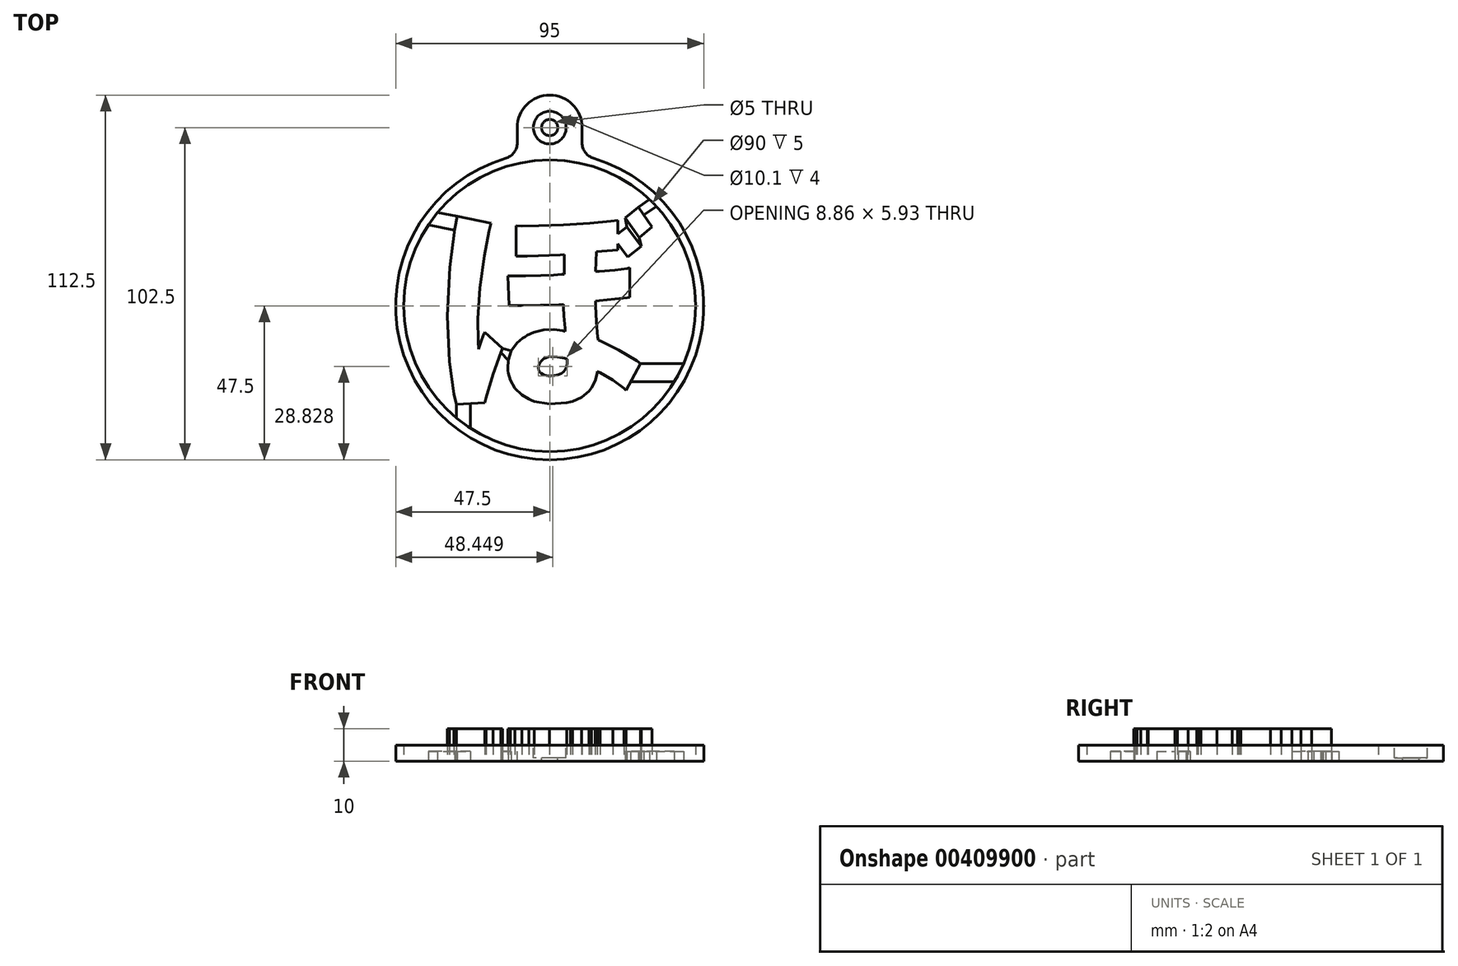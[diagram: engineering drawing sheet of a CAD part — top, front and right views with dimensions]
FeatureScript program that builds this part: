
annotation { "Feature Type Name" : "Feature", "Feature Type Description" : "" }
export const myFeature = defineFeature(function(context is Context, id is Id, definition is map)
    precondition{}
    {
        {
            var Q0;
            Q0=qCreatedBy(makeId("Top.planeOp"),FACE);
            var sketch = newSketch(context, id + "F0", { "sketchPlane" : qUnion([Q0])});
            skCircle(sketch, "E0", {"center": v(0, 0) * mm, "radius": 45 * mm});
            skCircle(sketch, "E1", {"center": v(0, 0) * mm, "radius": 47.5 * mm});
            skSolve(sketch);
        }
        {
            var Q0;
            Q0=qCreatedBy(makeId("Top.planeOp"),FACE);
            var sketch = newSketch(context, id + "F1", { "sketchPlane" : qUnion([Q0])});
            skLineSegment(sketch, "E2", {"start": v(27.39, 30.45) * mm, "end": v(31.52, 24.4) * mm});
            skLineSegment(sketch, "E3", {"start": v(31.52, 24.4) * mm, "end": v(27.67, 21.08) * mm});
            skLineSegment(sketch, "E4", {"start": v(27.67, 21.08) * mm, "end": v(23.26, 27.15) * mm});
            skLineSegment(sketch, "E5", {"start": v(23.26, 27.15) * mm, "end": v(27.39, 30.45) * mm});
            skLineSegment(sketch, "E6", {"start": v(-10.37, 24.67) * mm, "end": v(-8.61, 24.63) * mm});
            skLineSegment(sketch, "E7", {"start": v(-8.61, 24.63) * mm, "end": v(-3.34, 24.67) * mm});
            skLineSegment(sketch, "E8", {"start": v(-3.34, 24.67) * mm, "end": v(4.24, 24.94) * mm});
            skLineSegment(sketch, "E9", {"start": v(4.24, 24.94) * mm, "end": v(12.37, 25.5) * mm});
            skLineSegment(sketch, "E10", {"start": v(12.37, 25.5) * mm, "end": v(18.88, 26.09) * mm});
            skLineSegment(sketch, "E11", {"start": v(18.88, 26.09) * mm, "end": v(21.05, 26.32) * mm});
            skLineSegment(sketch, "E12", {"start": v(21.05, 26.32) * mm, "end": v(21.05, 22.19) * mm});
            skLineSegment(sketch, "E13", {"start": v(21.05, 22.19) * mm, "end": v(23.8, 24.4) * mm});
            skLineSegment(sketch, "E14", {"start": v(23.8, 24.4) * mm, "end": v(28.22, 18.33) * mm});
            skLineSegment(sketch, "E15", {"start": v(28.22, 18.33) * mm, "end": v(24.08, 15.02) * mm});
            skLineSegment(sketch, "E16", {"start": v(24.08, 15.02) * mm, "end": v(21.05, 19.15) * mm});
            skLineSegment(sketch, "E17", {"start": v(21.05, 19.15) * mm, "end": v(21.05, 17.23) * mm});
            skLineSegment(sketch, "E18", {"start": v(21.05, 17.23) * mm, "end": v(14.44, 16.67) * mm});
            skLineSegment(sketch, "E19", {"start": v(14.44, 16.67) * mm, "end": v(14.16, 10.61) * mm});
            skLineSegment(sketch, "E20", {"start": v(14.16, 10.61) * mm, "end": v(15.26, 10.66) * mm});
            skLineSegment(sketch, "E21", {"start": v(15.26, 10.66) * mm, "end": v(20.08, 11.02) * mm});
            skLineSegment(sketch, "E22", {"start": v(20.08, 11.02) * mm, "end": v(23.99, 11.58) * mm});
            skLineSegment(sketch, "E23", {"start": v(23.99, 11.58) * mm, "end": v(24.63, 11.71) * mm});
            skLineSegment(sketch, "E24", {"start": v(24.63, 11.71) * mm, "end": v(24.63, 2.62) * mm});
            skLineSegment(sketch, "E25", {"start": v(24.63, 2.62) * mm, "end": v(23.99, 2.53) * mm});
            skLineSegment(sketch, "E26", {"start": v(23.99, 2.53) * mm, "end": v(20.08, 2.07) * mm});
            skLineSegment(sketch, "E27", {"start": v(20.08, 2.07) * mm, "end": v(15.26, 1.6) * mm});
            skLineSegment(sketch, "E28", {"start": v(15.26, 1.6) * mm, "end": v(14.16, 1.52) * mm});
            skLineSegment(sketch, "E29", {"start": v(14.16, 1.52) * mm, "end": v(14.16, -0.07) * mm});
            skLineSegment(sketch, "E30", {"start": v(14.16, -0.07) * mm, "end": v(14.37, -4.82) * mm});
            skLineSegment(sketch, "E31", {"start": v(14.37, -4.82) * mm, "end": v(14.85, -9.7) * mm});
            skLineSegment(sketch, "E32", {"start": v(14.85, -9.7) * mm, "end": v(14.99, -10.61) * mm});
            skLineSegment(sketch, "E33", {"start": v(14.99, -10.61) * mm, "end": v(16, -11.02) * mm});
            skLineSegment(sketch, "E34", {"start": v(16, -11.02) * mm, "end": v(21.26, -13.64) * mm});
            skLineSegment(sketch, "E35", {"start": v(21.26, -13.64) * mm, "end": v(26.8, -17) * mm});
            skLineSegment(sketch, "E36", {"start": v(26.8, -17) * mm, "end": v(27.94, -17.78) * mm});
            skLineSegment(sketch, "E37", {"start": v(27.94, -17.78) * mm, "end": v(23.53, -26.04) * mm});
            skLineSegment(sketch, "E38", {"start": v(23.53, -26.04) * mm, "end": v(22.93, -25.5) * mm});
            skLineSegment(sketch, "E39", {"start": v(22.93, -25.5) * mm, "end": v(19.53, -22.94) * mm});
            skLineSegment(sketch, "E40", {"start": v(19.53, -22.94) * mm, "end": v(15.58, -20.67) * mm});
            skLineSegment(sketch, "E41", {"start": v(15.58, -20.67) * mm, "end": v(14.71, -20.26) * mm});
            skLineSegment(sketch, "E42", {"start": v(14.71, -20.26) * mm, "end": v(14.66, -20.76) * mm});
            skLineSegment(sketch, "E43", {"start": v(14.66, -20.76) * mm, "end": v(14.02, -23.15) * mm});
            skLineSegment(sketch, "E44", {"start": v(14.02, -23.15) * mm, "end": v(12.83, -25.36) * mm});
            skLineSegment(sketch, "E45", {"start": v(12.83, -25.36) * mm, "end": v(12.5, -25.77) * mm});
            skLineSegment(sketch, "E46", {"start": v(12.5, -25.77) * mm, "end": v(12.14, -26.27) * mm});
            skLineSegment(sketch, "E47", {"start": v(12.14, -26.27) * mm, "end": v(9.89, -28.25) * mm});
            skLineSegment(sketch, "E48", {"start": v(9.89, -28.25) * mm, "end": v(7.09, -29.49) * mm});
            skLineSegment(sketch, "E49", {"start": v(7.09, -29.49) * mm, "end": v(6.44, -29.63) * mm});
            skLineSegment(sketch, "E50", {"start": v(6.44, -29.63) * mm, "end": v(5.3, -29.9) * mm});
            skLineSegment(sketch, "E51", {"start": v(5.3, -29.9) * mm, "end": v(-0.04, -30.32) * mm});
            skLineSegment(sketch, "E52", {"start": v(-0.04, -30.32) * mm, "end": v(-4.81, -29.44) * mm});
            skLineSegment(sketch, "E53", {"start": v(-4.81, -29.44) * mm, "end": v(-5.68, -29.08) * mm});
            skLineSegment(sketch, "E54", {"start": v(-5.68, -29.08) * mm, "end": v(-6.45, -28.76) * mm});
            skLineSegment(sketch, "E55", {"start": v(-6.45, -28.76) * mm, "end": v(-8.61, -27.47) * mm});
            skLineSegment(sketch, "E56", {"start": v(-8.61, -27.47) * mm, "end": v(-10.78, -25.42) * mm});
            skLineSegment(sketch, "E57", {"start": v(-10.78, -25.42) * mm, "end": v(-12.2, -22.93) * mm});
            skLineSegment(sketch, "E58", {"start": v(-12.2, -22.93) * mm, "end": v(-12.79, -20.73) * mm});
            skLineSegment(sketch, "E59", {"start": v(-12.79, -20.73) * mm, "end": v(-12.85, -19.98) * mm});
            skLineSegment(sketch, "E60", {"start": v(-12.85, -19.98) * mm, "end": v(-12.91, -19.18) * mm});
            skLineSegment(sketch, "E61", {"start": v(-12.91, -19.18) * mm, "end": v(-12.73, -16.74) * mm});
            skLineSegment(sketch, "E62", {"start": v(-12.73, -16.74) * mm, "end": v(-11.82, -13.92) * mm});
            skLineSegment(sketch, "E63", {"start": v(-11.82, -13.92) * mm, "end": v(-10.11, -11.5) * mm});
            skLineSegment(sketch, "E64", {"start": v(-10.11, -11.5) * mm, "end": v(-8.29, -9.93) * mm});
            skLineSegment(sketch, "E65", {"start": v(-8.29, -9.93) * mm, "end": v(-7.61, -9.5) * mm});
            skLineSegment(sketch, "E66", {"start": v(-7.61, -9.5) * mm, "end": v(-6.97, -9.1) * mm});
            skLineSegment(sketch, "E67", {"start": v(-6.97, -9.1) * mm, "end": v(-4.87, -8.16) * mm});
            skLineSegment(sketch, "E68", {"start": v(-4.87, -8.16) * mm, "end": v(-1.9, -7.44) * mm});
            skLineSegment(sketch, "E69", {"start": v(-1.9, -7.44) * mm, "end": v(1.33, -7.34) * mm});
            skLineSegment(sketch, "E70", {"start": v(1.33, -7.34) * mm, "end": v(3.94, -7.66) * mm});
            skLineSegment(sketch, "E71", {"start": v(3.94, -7.66) * mm, "end": v(4.79, -7.85) * mm});
            skLineSegment(sketch, "E72", {"start": v(4.79, -7.85) * mm, "end": v(4.7, -6.94) * mm});
            skLineSegment(sketch, "E73", {"start": v(4.7, -6.94) * mm, "end": v(4.37, -3.03) * mm});
            skLineSegment(sketch, "E74", {"start": v(4.37, -3.03) * mm, "end": v(4.24, -0.45) * mm});
            skLineSegment(sketch, "E75", {"start": v(4.24, -0.45) * mm, "end": v(4.24, 0.41) * mm});
            skLineSegment(sketch, "E76", {"start": v(4.24, 0.41) * mm, "end": v(2.81, 0.37) * mm});
            skLineSegment(sketch, "E77", {"start": v(2.81, 0.37) * mm, "end": v(-8.73, 0.14) * mm});
            skLineSegment(sketch, "E78", {"start": v(-8.73, 0.14) * mm, "end": v(-12.57, 0.14) * mm});
            skLineSegment(sketch, "E79", {"start": v(-12.57, 0.14) * mm, "end": v(-12.85, 9.23) * mm});
            skLineSegment(sketch, "E80", {"start": v(-12.85, 9.23) * mm, "end": v(-11.5, 9.23) * mm});
            skLineSegment(sketch, "E81", {"start": v(-11.5, 9.23) * mm, "end": v(-7.42, 9.27) * mm});
            skLineSegment(sketch, "E82", {"start": v(-7.42, 9.27) * mm, "end": v(-2.72, 9.37) * mm});
            skLineSegment(sketch, "E83", {"start": v(-2.72, 9.37) * mm, "end": v(1.26, 9.54) * mm});
            skLineSegment(sketch, "E84", {"start": v(1.26, 9.54) * mm, "end": v(3.7, 9.7) * mm});
            skLineSegment(sketch, "E85", {"start": v(3.7, 9.7) * mm, "end": v(4.51, 9.78) * mm});
            skLineSegment(sketch, "E86", {"start": v(4.51, 9.78) * mm, "end": v(4.51, 15.85) * mm});
            skLineSegment(sketch, "E87", {"start": v(4.51, 15.85) * mm, "end": v(3.27, 15.76) * mm});
            skLineSegment(sketch, "E88", {"start": v(3.27, 15.76) * mm, "end": v(-6.96, 15.3) * mm});
            skLineSegment(sketch, "E89", {"start": v(-6.96, 15.3) * mm, "end": v(-10.37, 15.3) * mm});
            skLineSegment(sketch, "E90", {"start": v(-10.37, 15.3) * mm, "end": v(-10.37, 24.67) * mm});
            skLineSegment(sketch, "E91", {"start": v(0.1, -21.63) * mm, "end": v(0.44, -21.63) * mm});
            skLineSegment(sketch, "E92", {"start": v(0.44, -21.63) * mm, "end": v(1.45, -21.55) * mm});
            skLineSegment(sketch, "E93", {"start": v(1.45, -21.55) * mm, "end": v(2.6, -21.3) * mm});
            skLineSegment(sketch, "E94", {"start": v(2.6, -21.3) * mm, "end": v(3.55, -20.9) * mm});
            skLineSegment(sketch, "E95", {"start": v(3.55, -20.9) * mm, "end": v(4.3, -20.33) * mm});
            skLineSegment(sketch, "E96", {"start": v(4.3, -20.33) * mm, "end": v(4.86, -19.59) * mm});
            skLineSegment(sketch, "E97", {"start": v(4.86, -19.59) * mm, "end": v(5.22, -18.69) * mm});
            skLineSegment(sketch, "E98", {"start": v(5.22, -18.69) * mm, "end": v(5.38, -17.63) * mm});
            skLineSegment(sketch, "E99", {"start": v(5.38, -17.63) * mm, "end": v(5.37, -16.7) * mm});
            skLineSegment(sketch, "E100", {"start": v(5.37, -16.7) * mm, "end": v(5.34, -16.4) * mm});
            skLineSegment(sketch, "E101", {"start": v(5.34, -16.4) * mm, "end": v(4.6, -16.18) * mm});
            skLineSegment(sketch, "E102", {"start": v(4.6, -16.18) * mm, "end": v(2.34, -15.74) * mm});
            skLineSegment(sketch, "E103", {"start": v(2.34, -15.74) * mm, "end": v(-0.03, -15.7) * mm});
            skLineSegment(sketch, "E104", {"start": v(-0.03, -15.7) * mm, "end": v(-1.8, -16.3) * mm});
            skLineSegment(sketch, "E105", {"start": v(-1.8, -16.3) * mm, "end": v(-2.74, -17.15) * mm});
            skLineSegment(sketch, "E106", {"start": v(-2.74, -17.15) * mm, "end": v(-2.93, -17.5) * mm});
            skLineSegment(sketch, "E107", {"start": v(-2.93, -17.5) * mm, "end": v(-3.05, -17.72) * mm});
            skLineSegment(sketch, "E108", {"start": v(-3.05, -17.72) * mm, "end": v(-3.34, -18.41) * mm});
            skLineSegment(sketch, "E109", {"start": v(-3.34, -18.41) * mm, "end": v(-3.48, -19.22) * mm});
            skLineSegment(sketch, "E110", {"start": v(-3.48, -19.22) * mm, "end": v(-3.34, -19.93) * mm});
            skLineSegment(sketch, "E111", {"start": v(-3.34, -19.93) * mm, "end": v(-3.06, -20.4) * mm});
            skLineSegment(sketch, "E112", {"start": v(-3.06, -20.4) * mm, "end": v(-2.93, -20.53) * mm});
            skLineSegment(sketch, "E113", {"start": v(-2.93, -20.53) * mm, "end": v(-2.79, -20.72) * mm});
            skLineSegment(sketch, "E114", {"start": v(-2.79, -20.72) * mm, "end": v(-1.76, -21.36) * mm});
            skLineSegment(sketch, "E115", {"start": v(-1.76, -21.36) * mm, "end": v(-0.36, -21.63) * mm});
            skLineSegment(sketch, "E116", {"start": v(-0.36, -21.63) * mm, "end": v(0.1, -21.63) * mm});
            skLineSegment(sketch, "E117", {"start": v(-28.83, -30.45) * mm, "end": v(-29.54, -27.18) * mm});
            skLineSegment(sketch, "E118", {"start": v(-29.54, -27.18) * mm, "end": v(-30.89, -17.2) * mm});
            skLineSegment(sketch, "E119", {"start": v(-30.89, -17.2) * mm, "end": v(-31.52, -3.1) * mm});
            skLineSegment(sketch, "E120", {"start": v(-31.52, -3.1) * mm, "end": v(-30.75, 11.87) * mm});
            skLineSegment(sketch, "E121", {"start": v(-30.75, 11.87) * mm, "end": v(-29.26, 23.77) * mm});
            skLineSegment(sketch, "E122", {"start": v(-29.26, 23.77) * mm, "end": v(-28.56, 27.7) * mm});
            skLineSegment(sketch, "E123", {"start": v(-28.56, 27.7) * mm, "end": v(-18.09, 25.5) * mm});
            skLineSegment(sketch, "E124", {"start": v(-18.09, 25.5) * mm, "end": v(-18.7, 23) * mm});
            skLineSegment(sketch, "E125", {"start": v(-18.7, 23) * mm, "end": v(-20.19, 15.42) * mm});
            skLineSegment(sketch, "E126", {"start": v(-20.19, 15.42) * mm, "end": v(-21.53, 5.58) * mm});
            skLineSegment(sketch, "E127", {"start": v(-21.53, 5.58) * mm, "end": v(-22.12, -4.01) * mm});
            skLineSegment(sketch, "E128", {"start": v(-22.12, -4.01) * mm, "end": v(-22.08, -11.03) * mm});
            skLineSegment(sketch, "E129", {"start": v(-22.08, -11.03) * mm, "end": v(-21.94, -13.37) * mm});
            skLineSegment(sketch, "E130", {"start": v(-21.94, -13.37) * mm, "end": v(-21.8, -12.86) * mm});
            skLineSegment(sketch, "E131", {"start": v(-21.8, -12.86) * mm, "end": v(-21.05, -10.54) * mm});
            skLineSegment(sketch, "E132", {"start": v(-21.05, -10.54) * mm, "end": v(-20.2, -8.5) * mm});
            skLineSegment(sketch, "E133", {"start": v(-20.2, -8.5) * mm, "end": v(-20.02, -8.13) * mm});
            skLineSegment(sketch, "E134", {"start": v(-20.02, -8.13) * mm, "end": v(-14.5, -13.1) * mm});
            skLineSegment(sketch, "E135", {"start": v(-14.5, -13.1) * mm, "end": v(-15.05, -14.38) * mm});
            skLineSegment(sketch, "E136", {"start": v(-15.05, -14.38) * mm, "end": v(-17.54, -21.15) * mm});
            skLineSegment(sketch, "E137", {"start": v(-17.54, -21.15) * mm, "end": v(-19.65, -28.39) * mm});
            skLineSegment(sketch, "E138", {"start": v(-19.65, -28.39) * mm, "end": v(-20.02, -29.9) * mm});
            skLineSegment(sketch, "E139", {"start": v(-20.02, -29.9) * mm, "end": v(-28.83, -30.45) * mm});
            skSolve(sketch);
        }
        {
            var Q0;
            Q0 = qSketchRegion(id + "F0", true);
            extrude(context, id + "F2", {"entities" : qUnion([Q0]), "depth" : 5 * mm});
        }
        {
            var Q0;
            Q0=makeQuery(id+"F1.imprint","IMPRINT",FACE,{"disambiguationData":[TD([[makeQuery(id+"F1.imprint","IMPRINT",EDGE,{"derivedFrom":sQuery(id+"F1.wireOp",EDGE,"E117")}),-1.0]])]});
            var Q1;
            Q1=makeQuery(id+"F1.imprint","IMPRINT",FACE,{"disambiguationData":[TD([[makeQuery(id+"F1.imprint","IMPRINT",EDGE,{"derivedFrom":sQuery(id+"F1.wireOp",EDGE,"E6")}),-1.0]])]});
            var Q2;
            Q2=makeQuery(id+"F1.imprint","IMPRINT",FACE,{"disambiguationData":[TD([[makeQuery(id+"F1.imprint","IMPRINT",EDGE,{"derivedFrom":sQuery(id+"F1.wireOp",EDGE,"E2")}),-1.0]])]});
            extrude(context, id + "F3", {"entities" : qUnion([Q0, Q1, Q2]), "depth" : 10 * mm});
        }
        {
            var Q0;
            Q0=makeQuery(id+"F2.opExtrude","CAP_FACE",FACE,{"disambiguationData":[OSD([sQuery(id+"F0.wireOp",EDGE,"E0"),sQuery(id+"F0.wireOp",EDGE,"E1")])],"isStart":true});
            var sketch = newSketch(context, id + "F4", { "sketchPlane" : qUnion([Q0])});
            skLineSegment(sketch, "E140.0.0", {"start": v(-20.02, 29.9) * mm, "end": v(-28.83, 30.45) * mm, "construction": true});
            skLineSegment(sketch, "E140.0.1", {"start": v(-28.83, 30.45) * mm, "end": v(-29.54, 27.18) * mm, "construction": true});
            skLineSegment(sketch, "E140.0.2", {"start": v(-29.54, 27.18) * mm, "end": v(-30.89, 17.2) * mm, "construction": true});
            skLineSegment(sketch, "E140.0.3", {"start": v(-30.89, 17.2) * mm, "end": v(-31.52, 3.1) * mm, "construction": true});
            skLineSegment(sketch, "E140.0.4", {"start": v(-31.52, 3.1) * mm, "end": v(-30.75, -11.87) * mm, "construction": true});
            skLineSegment(sketch, "E140.0.5", {"start": v(-30.75, -11.87) * mm, "end": v(-29.26, -23.77) * mm, "construction": true});
            skLineSegment(sketch, "E140.0.6", {"start": v(-29.26, -23.77) * mm, "end": v(-28.56, -27.7) * mm, "construction": true});
            skLineSegment(sketch, "E140.0.7", {"start": v(-28.56, -27.7) * mm, "end": v(-18.09, -25.5) * mm, "construction": true});
            skLineSegment(sketch, "E140.0.8", {"start": v(-18.09, -25.5) * mm, "end": v(-18.7, -23) * mm, "construction": true});
            skLineSegment(sketch, "E140.0.9", {"start": v(-18.7, -23) * mm, "end": v(-20.19, -15.42) * mm, "construction": true});
            skLineSegment(sketch, "E140.0.10", {"start": v(-20.19, -15.42) * mm, "end": v(-21.53, -5.58) * mm, "construction": true});
            skLineSegment(sketch, "E140.0.11", {"start": v(-21.53, -5.58) * mm, "end": v(-22.12, 4.01) * mm, "construction": true});
            skLineSegment(sketch, "E140.0.12", {"start": v(-22.12, 4.01) * mm, "end": v(-22.08, 11.03) * mm, "construction": true});
            skLineSegment(sketch, "E140.0.13", {"start": v(-22.08, 11.03) * mm, "end": v(-21.94, 13.37) * mm, "construction": true});
            skLineSegment(sketch, "E140.0.14", {"start": v(-21.94, 13.37) * mm, "end": v(-21.8, 12.86) * mm, "construction": true});
            skLineSegment(sketch, "E140.0.15", {"start": v(-21.8, 12.86) * mm, "end": v(-21.05, 10.54) * mm, "construction": true});
            skLineSegment(sketch, "E140.0.16", {"start": v(-21.05, 10.54) * mm, "end": v(-20.2, 8.5) * mm, "construction": true});
            skLineSegment(sketch, "E140.0.17", {"start": v(-20.2, 8.5) * mm, "end": v(-20.02, 8.13) * mm, "construction": true});
            skLineSegment(sketch, "E140.0.18", {"start": v(-20.02, 8.13) * mm, "end": v(-14.5, 13.1) * mm, "construction": true});
            skLineSegment(sketch, "E140.0.19", {"start": v(-14.5, 13.1) * mm, "end": v(-15.05, 14.38) * mm, "construction": true});
            skLineSegment(sketch, "E140.0.20", {"start": v(-15.05, 14.38) * mm, "end": v(-17.54, 21.15) * mm, "construction": true});
            skLineSegment(sketch, "E140.0.21", {"start": v(-17.54, 21.15) * mm, "end": v(-19.65, 28.39) * mm, "construction": true});
            skLineSegment(sketch, "E140.0.22", {"start": v(-19.65, 28.39) * mm, "end": v(-20.02, 29.9) * mm, "construction": true});
            skLineSegment(sketch, "E141.0.0", {"start": v(-10.37, -15.3) * mm, "end": v(-10.37, -24.67) * mm, "construction": true});
            skLineSegment(sketch, "E141.0.1", {"start": v(-10.37, -24.67) * mm, "end": v(-8.61, -24.63) * mm, "construction": true});
            skLineSegment(sketch, "E141.0.2", {"start": v(-8.61, -24.63) * mm, "end": v(-3.34, -24.67) * mm, "construction": true});
            skLineSegment(sketch, "E141.0.3", {"start": v(-3.34, -24.67) * mm, "end": v(4.24, -24.94) * mm, "construction": true});
            skLineSegment(sketch, "E141.0.4", {"start": v(4.24, -24.94) * mm, "end": v(12.37, -25.5) * mm, "construction": true});
            skLineSegment(sketch, "E141.0.5", {"start": v(12.37, -25.5) * mm, "end": v(18.88, -26.09) * mm, "construction": true});
            skLineSegment(sketch, "E141.0.6", {"start": v(18.88, -26.09) * mm, "end": v(21.05, -26.32) * mm, "construction": true});
            skLineSegment(sketch, "E141.0.7", {"start": v(21.05, -26.32) * mm, "end": v(21.05, -22.19) * mm, "construction": true});
            skLineSegment(sketch, "E141.0.8", {"start": v(21.05, -22.19) * mm, "end": v(23.8, -24.4) * mm, "construction": true});
            skLineSegment(sketch, "E141.0.9", {"start": v(23.8, -24.4) * mm, "end": v(28.22, -18.33) * mm, "construction": true});
            skLineSegment(sketch, "E141.0.10", {"start": v(28.22, -18.33) * mm, "end": v(24.08, -15.02) * mm, "construction": true});
            skLineSegment(sketch, "E141.0.11", {"start": v(24.08, -15.02) * mm, "end": v(21.05, -19.15) * mm, "construction": true});
            skLineSegment(sketch, "E141.0.12", {"start": v(21.05, -19.15) * mm, "end": v(21.05, -17.23) * mm, "construction": true});
            skLineSegment(sketch, "E141.0.13", {"start": v(21.05, -17.23) * mm, "end": v(14.44, -16.67) * mm, "construction": true});
            skLineSegment(sketch, "E141.0.14", {"start": v(14.44, -16.67) * mm, "end": v(14.16, -10.61) * mm, "construction": true});
            skLineSegment(sketch, "E141.0.15", {"start": v(14.16, -10.61) * mm, "end": v(15.26, -10.66) * mm, "construction": true});
            skLineSegment(sketch, "E141.0.16", {"start": v(15.26, -10.66) * mm, "end": v(20.08, -11.02) * mm, "construction": true});
            skLineSegment(sketch, "E141.0.17", {"start": v(20.08, -11.02) * mm, "end": v(23.99, -11.58) * mm, "construction": true});
            skLineSegment(sketch, "E141.0.18", {"start": v(23.99, -11.58) * mm, "end": v(24.63, -11.71) * mm, "construction": true});
            skLineSegment(sketch, "E141.0.19", {"start": v(24.63, -11.71) * mm, "end": v(24.63, -2.62) * mm, "construction": true});
            skLineSegment(sketch, "E141.0.20", {"start": v(24.63, -2.62) * mm, "end": v(23.99, -2.53) * mm, "construction": true});
            skLineSegment(sketch, "E141.0.21", {"start": v(23.99, -2.53) * mm, "end": v(20.08, -2.07) * mm, "construction": true});
            skLineSegment(sketch, "E141.0.22", {"start": v(20.08, -2.07) * mm, "end": v(15.26, -1.6) * mm, "construction": true});
            skLineSegment(sketch, "E141.0.23", {"start": v(15.26, -1.6) * mm, "end": v(14.16, -1.52) * mm, "construction": true});
            skLineSegment(sketch, "E141.0.24", {"start": v(14.16, -1.52) * mm, "end": v(14.16, 0.07) * mm, "construction": true});
            skLineSegment(sketch, "E141.0.25", {"start": v(14.16, 0.07) * mm, "end": v(14.37, 4.82) * mm, "construction": true});
            skLineSegment(sketch, "E141.0.26", {"start": v(14.37, 4.82) * mm, "end": v(14.85, 9.7) * mm, "construction": true});
            skLineSegment(sketch, "E141.0.27", {"start": v(14.85, 9.7) * mm, "end": v(14.99, 10.61) * mm, "construction": true});
            skLineSegment(sketch, "E141.0.28", {"start": v(14.99, 10.61) * mm, "end": v(16, 11.02) * mm, "construction": true});
            skLineSegment(sketch, "E141.0.29", {"start": v(16, 11.02) * mm, "end": v(21.26, 13.64) * mm, "construction": true});
            skLineSegment(sketch, "E141.0.30", {"start": v(21.26, 13.64) * mm, "end": v(26.8, 17) * mm, "construction": true});
            skLineSegment(sketch, "E141.0.31", {"start": v(26.8, 17) * mm, "end": v(27.94, 17.78) * mm, "construction": true});
            skLineSegment(sketch, "E141.0.32", {"start": v(27.94, 17.78) * mm, "end": v(23.53, 26.04) * mm, "construction": true});
            skLineSegment(sketch, "E141.0.33", {"start": v(23.53, 26.04) * mm, "end": v(22.93, 25.5) * mm, "construction": true});
            skLineSegment(sketch, "E141.0.34", {"start": v(22.93, 25.5) * mm, "end": v(19.53, 22.94) * mm, "construction": true});
            skLineSegment(sketch, "E141.0.35", {"start": v(19.53, 22.94) * mm, "end": v(15.58, 20.67) * mm, "construction": true});
            skLineSegment(sketch, "E141.0.36", {"start": v(15.58, 20.67) * mm, "end": v(14.71, 20.26) * mm, "construction": true});
            skLineSegment(sketch, "E141.0.37", {"start": v(14.71, 20.26) * mm, "end": v(14.66, 20.76) * mm, "construction": true});
            skLineSegment(sketch, "E141.0.38", {"start": v(14.66, 20.76) * mm, "end": v(14.02, 23.15) * mm, "construction": true});
            skLineSegment(sketch, "E141.0.39", {"start": v(14.02, 23.15) * mm, "end": v(12.83, 25.36) * mm, "construction": true});
            skLineSegment(sketch, "E141.0.40", {"start": v(12.83, 25.36) * mm, "end": v(12.5, 25.77) * mm, "construction": true});
            skLineSegment(sketch, "E141.0.41", {"start": v(12.5, 25.77) * mm, "end": v(12.14, 26.27) * mm, "construction": true});
            skLineSegment(sketch, "E141.0.42", {"start": v(12.14, 26.27) * mm, "end": v(9.89, 28.25) * mm, "construction": true});
            skLineSegment(sketch, "E141.0.43", {"start": v(9.89, 28.25) * mm, "end": v(7.09, 29.49) * mm, "construction": true});
            skLineSegment(sketch, "E141.0.44", {"start": v(7.09, 29.49) * mm, "end": v(6.44, 29.63) * mm, "construction": true});
            skLineSegment(sketch, "E141.0.45", {"start": v(6.44, 29.63) * mm, "end": v(5.3, 29.9) * mm, "construction": true});
            skLineSegment(sketch, "E141.0.46", {"start": v(5.3, 29.9) * mm, "end": v(-0.04, 30.32) * mm, "construction": true});
            skLineSegment(sketch, "E141.0.47", {"start": v(-0.04, 30.32) * mm, "end": v(-4.81, 29.44) * mm, "construction": true});
            skLineSegment(sketch, "E141.0.48", {"start": v(-4.81, 29.44) * mm, "end": v(-5.68, 29.08) * mm, "construction": true});
            skLineSegment(sketch, "E141.0.49", {"start": v(-5.68, 29.08) * mm, "end": v(-6.45, 28.76) * mm, "construction": true});
            skLineSegment(sketch, "E141.0.50", {"start": v(-6.45, 28.76) * mm, "end": v(-8.61, 27.47) * mm, "construction": true});
            skLineSegment(sketch, "E141.0.51", {"start": v(-8.61, 27.47) * mm, "end": v(-10.78, 25.42) * mm, "construction": true});
            skLineSegment(sketch, "E141.0.52", {"start": v(-10.78, 25.42) * mm, "end": v(-12.2, 22.93) * mm, "construction": true});
            skLineSegment(sketch, "E141.0.53", {"start": v(-12.2, 22.93) * mm, "end": v(-12.79, 20.73) * mm, "construction": true});
            skLineSegment(sketch, "E141.0.54", {"start": v(-12.79, 20.73) * mm, "end": v(-12.85, 19.98) * mm, "construction": true});
            skLineSegment(sketch, "E141.0.55", {"start": v(-12.85, 19.98) * mm, "end": v(-12.91, 19.18) * mm, "construction": true});
            skLineSegment(sketch, "E141.0.56", {"start": v(-12.91, 19.18) * mm, "end": v(-12.73, 16.74) * mm, "construction": true});
            skLineSegment(sketch, "E141.0.57", {"start": v(-12.73, 16.74) * mm, "end": v(-11.82, 13.92) * mm, "construction": true});
            skLineSegment(sketch, "E141.0.58", {"start": v(-11.82, 13.92) * mm, "end": v(-10.11, 11.5) * mm, "construction": true});
            skLineSegment(sketch, "E141.0.59", {"start": v(-10.11, 11.5) * mm, "end": v(-8.29, 9.93) * mm, "construction": true});
            skLineSegment(sketch, "E141.0.60", {"start": v(-8.29, 9.93) * mm, "end": v(-7.61, 9.5) * mm, "construction": true});
            skLineSegment(sketch, "E141.0.61", {"start": v(-7.61, 9.5) * mm, "end": v(-6.97, 9.1) * mm, "construction": true});
            skLineSegment(sketch, "E141.0.62", {"start": v(-6.97, 9.1) * mm, "end": v(-4.87, 8.16) * mm, "construction": true});
            skLineSegment(sketch, "E141.0.63", {"start": v(-4.87, 8.16) * mm, "end": v(-1.9, 7.44) * mm, "construction": true});
            skLineSegment(sketch, "E141.0.64", {"start": v(-1.9, 7.44) * mm, "end": v(1.33, 7.34) * mm, "construction": true});
            skLineSegment(sketch, "E141.0.65", {"start": v(1.33, 7.34) * mm, "end": v(3.94, 7.66) * mm, "construction": true});
            skLineSegment(sketch, "E141.0.66", {"start": v(3.94, 7.66) * mm, "end": v(4.79, 7.85) * mm, "construction": true});
            skLineSegment(sketch, "E141.0.67", {"start": v(4.79, 7.85) * mm, "end": v(4.7, 6.94) * mm, "construction": true});
            skLineSegment(sketch, "E141.0.68", {"start": v(4.7, 6.94) * mm, "end": v(4.37, 3.03) * mm, "construction": true});
            skLineSegment(sketch, "E141.0.69", {"start": v(4.37, 3.03) * mm, "end": v(4.24, 0.45) * mm, "construction": true});
            skLineSegment(sketch, "E141.0.70", {"start": v(4.24, 0.45) * mm, "end": v(4.24, -0.41) * mm, "construction": true});
            skLineSegment(sketch, "E141.0.71", {"start": v(4.24, -0.41) * mm, "end": v(2.81, -0.37) * mm, "construction": true});
            skLineSegment(sketch, "E141.0.72", {"start": v(2.81, -0.37) * mm, "end": v(-8.73, -0.14) * mm, "construction": true});
            skLineSegment(sketch, "E141.0.73", {"start": v(-8.73, -0.14) * mm, "end": v(-12.57, -0.14) * mm, "construction": true});
            skLineSegment(sketch, "E141.0.74", {"start": v(-12.57, -0.14) * mm, "end": v(-12.85, -9.23) * mm, "construction": true});
            skLineSegment(sketch, "E141.0.75", {"start": v(-12.85, -9.23) * mm, "end": v(-11.5, -9.23) * mm, "construction": true});
            skLineSegment(sketch, "E141.0.76", {"start": v(-11.5, -9.23) * mm, "end": v(-7.42, -9.27) * mm, "construction": true});
            skLineSegment(sketch, "E141.0.77", {"start": v(-7.42, -9.27) * mm, "end": v(-2.72, -9.37) * mm, "construction": true});
            skLineSegment(sketch, "E141.0.78", {"start": v(-2.72, -9.37) * mm, "end": v(1.26, -9.54) * mm, "construction": true});
            skLineSegment(sketch, "E141.0.79", {"start": v(1.26, -9.54) * mm, "end": v(3.7, -9.7) * mm, "construction": true});
            skLineSegment(sketch, "E141.0.80", {"start": v(3.7, -9.7) * mm, "end": v(4.51, -9.78) * mm, "construction": true});
            skLineSegment(sketch, "E141.0.81", {"start": v(4.51, -9.78) * mm, "end": v(4.51, -15.85) * mm, "construction": true});
            skLineSegment(sketch, "E141.0.82", {"start": v(4.51, -15.85) * mm, "end": v(3.27, -15.76) * mm, "construction": true});
            skLineSegment(sketch, "E141.0.83", {"start": v(3.27, -15.76) * mm, "end": v(-6.96, -15.3) * mm, "construction": true});
            skLineSegment(sketch, "E141.0.84", {"start": v(-6.96, -15.3) * mm, "end": v(-10.37, -15.3) * mm, "construction": true});
            skLineSegment(sketch, "E142.0.0", {"start": v(23.26, -27.15) * mm, "end": v(27.39, -30.45) * mm, "construction": true});
            skLineSegment(sketch, "E142.0.1", {"start": v(27.39, -30.45) * mm, "end": v(31.52, -24.4) * mm, "construction": true});
            skLineSegment(sketch, "E142.0.2", {"start": v(31.52, -24.4) * mm, "end": v(27.67, -21.08) * mm, "construction": true});
            skLineSegment(sketch, "E142.0.3", {"start": v(27.67, -21.08) * mm, "end": v(23.26, -27.15) * mm, "construction": true});
            skLineSegment(sketch, "E143", {"start": v(-28.83, 30.45) * mm, "end": v(-28.83, 37.75) * mm});
            skLineSegment(sketch, "E144", {"start": v(-28.83, 37.75) * mm, "end": v(-24.5, 37.75) * mm});
            skLineSegment(sketch, "E145", {"start": v(-24.5, 37.75) * mm, "end": v(-24.5, 30.18) * mm});
            skPoint(sketch, "E145.endSnap0", {"position": v(-24.43, 30.18) * mm});
            skLineSegment(sketch, "E146", {"start": v(-24.5, 30.18) * mm, "end": v(-28.83, 30.45) * mm});
            skLineSegment(sketch, "E147", {"start": v(27.94, 17.78) * mm, "end": v(41.34, 17.78) * mm});
            skLineSegment(sketch, "E148", {"start": v(41.34, 17.78) * mm, "end": v(41.34, 23.4) * mm});
            skLineSegment(sketch, "E149", {"start": v(41.34, 23.4) * mm, "end": v(24.94, 23.4) * mm});
            skLineSegment(sketch, "E150", {"start": v(24.94, 23.4) * mm, "end": v(27.94, 17.78) * mm});
            skLineSegment(sketch, "E151", {"start": v(28.22, -18.33) * mm, "end": v(27.67, -21.08) * mm});
            skLineSegment(sketch, "E152", {"start": v(23.26, -27.15) * mm, "end": v(23.8, -24.4) * mm});
            skLineSegment(sketch, "E153", {"start": v(28.22, -18.33) * mm, "end": v(23.8, -24.4) * mm});
            skLineSegment(sketch, "E154", {"start": v(23.26, -27.15) * mm, "end": v(27.67, -21.08) * mm});
            skLineSegment(sketch, "E155", {"start": v(-28.56, -27.7) * mm, "end": v(-37.4, -29.27) * mm});
            skLineSegment(sketch, "E156", {"start": v(-37.4, -29.27) * mm, "end": v(-37.4, -25.02) * mm});
            skLineSegment(sketch, "E157", {"start": v(-37.4, -25.02) * mm, "end": v(-29.26, -23.3) * mm});
            skLineSegment(sketch, "E158", {"start": v(-28.56, -27.7) * mm, "end": v(-29.26, -23.3) * mm});
            skLineSegment(sketch, "E159", {"start": v(-14.5, 13.1) * mm, "end": v(-15.05, 14.38) * mm});
            skLineSegment(sketch, "E160", {"start": v(-15.05, 14.38) * mm, "end": v(-12.73, 16.74) * mm});
            skLineSegment(sketch, "E161", {"start": v(-12.73, 16.74) * mm, "end": v(-11.82, 13.92) * mm});
            skLineSegment(sketch, "E162", {"start": v(-11.82, 13.92) * mm, "end": v(-14.5, 13.1) * mm});
            skLineSegment(sketch, "E163", {"start": v(27.39, -30.45) * mm, "end": v(32.93, -34.23) * mm});
            skLineSegment(sketch, "E164", {"start": v(32.93, -34.23) * mm, "end": v(32.93, -30.67) * mm});
            skLineSegment(sketch, "E165", {"start": v(32.93, -30.67) * mm, "end": v(29.05, -28.02) * mm});
            skLineSegment(sketch, "E166", {"start": v(29.05, -28.02) * mm, "end": v(27.39, -30.45) * mm});
            skSolve(sketch);
        }
        {
            var Q0;
            {var subQ4=sQuery(id+"F4.wireOp",EDGE,"E157");Q0=makeQuery(id+"F4.imprint","IMPRINT",FACE,{"disambiguationData":[TD([[makeQuery(id+"F4.imprint","IMPRINT",EDGE,{"derivedFrom":subQ4}),-1.0]])]});}
            var Q1;
            {var subQ4=sQuery(id+"F4.wireOp",EDGE,"E145");Q1=makeQuery(id+"F4.imprint","IMPRINT",FACE,{"disambiguationData":[TD([[makeQuery(id+"F4.imprint","IMPRINT",EDGE,{"derivedFrom":subQ4}),-1.0]])]});}
            var Q2;
            Q2=makeQuery(id+"F4.imprint","IMPRINT",FACE,{"disambiguationData":[TD([[makeQuery(id+"F4.imprint","IMPRINT",EDGE,{"derivedFrom":sQuery(id+"F4.wireOp",EDGE,"E159")}),-1.0]])]});
            var Q3;
            {var subQ0=sQuery(id+"F4.wireOp",EDGE,"E147");Q3=makeQuery(id+"F4.imprint","IMPRINT",FACE,{"disambiguationData":[TD([[makeQuery(id+"F4.imprint","IMPRINT",EDGE,{"derivedFrom":subQ0}),1.0]])]});}
            var Q4;
            Q4=makeQuery(id+"F4.imprint","IMPRINT",FACE,{"disambiguationData":[TD([[makeQuery(id+"F4.imprint","IMPRINT",EDGE,{"derivedFrom":sQuery(id+"F4.wireOp",EDGE,"E151")}),-1.0]])]});
            var Q5;
            {var subQ4=sQuery(id+"F4.wireOp",EDGE,"E165");Q5=makeQuery(id+"F4.imprint","IMPRINT",FACE,{"disambiguationData":[TD([[makeQuery(id+"F4.imprint","IMPRINT",EDGE,{"derivedFrom":subQ4}),1.0]])]});}
            extrude(context, id + "F5", {"entities" : qUnion([Q0, Q1, Q2, Q3, Q4, Q5]), "oppositeDirection" : true, "depth" : 3 * mm});
        }
        {
            var Q0;
            Q0=qCreatedBy(makeId("Top.planeOp"),FACE);
            var sketch = newSketch(context, id + "F6", { "sketchPlane" : qUnion([Q0])});
            skCircle(sketch, "E167", {"center": v(0, 55) * mm, "radius": 10 * mm});
            skArc(sketch, "E168.0", {"start": v(10, 43.87) * mm, "mid": v(0, 45) * mm, "end": v(-10, 43.87) * mm});
            skPoint(sketch, "E169", {"position": v(0, 45) * mm});
            skLineSegment(sketch, "E170.bottom", {"start": v(-10, 55) * mm, "end": v(10, 55) * mm});
            skLineSegment(sketch, "E170.top", {"start": v(-10, 43.87) * mm, "end": v(10, 43.87) * mm});
            skLineSegment(sketch, "E170.left", {"start": v(-10, 55) * mm, "end": v(-10, 43.87) * mm});
            skLineSegment(sketch, "E170.right", {"start": v(10, 55) * mm, "end": v(10, 43.87) * mm});
            skSolve(sketch);
        }
        {
            var Q0;
            {var subQ0=sQuery(id+"F6.wireOp",EDGE,"E170.left");Q0=makeQuery(id+"F6.imprint","IMPRINT",FACE,{"disambiguationData":[TD([[makeQuery(id+"F6.imprint","IMPRINT",EDGE,{"derivedFrom":subQ0}),1.0]])]});}
            var Q1;
            {var subQ0=sQuery(id+"F6.wireOp",EDGE,"E170.right");Q1=makeQuery(id+"F6.imprint","IMPRINT",FACE,{"disambiguationData":[TD([[makeQuery(id+"F6.imprint","IMPRINT",EDGE,{"derivedFrom":subQ0}),-1.0]])]});}
            var Q2;
            {var subQ0=sQuery(id+"F6.wireOp",EDGE,"E170.bottom");Q2=makeQuery(id+"F6.imprint","IMPRINT",FACE,{"disambiguationData":[TD([[makeQuery(id+"F6.imprint","IMPRINT",EDGE,{"derivedFrom":subQ0}),-1.0]])]});}
            var Q3;
            {var subQ0=sQuery(id+"F6.wireOp",EDGE,"E170.bottom");Q3=makeQuery(id+"F6.imprint","IMPRINT",FACE,{"disambiguationData":[TD([[makeQuery(id+"F6.imprint","IMPRINT",EDGE,{"derivedFrom":subQ0}),1.0]])]});}
            var Q4;
            Q4=makeQuery(id+"F2.opExtrude","CAP_FACE",FACE,{"disambiguationData":[OSD([sQuery(id+"F0.wireOp",EDGE,"E0"),sQuery(id+"F0.wireOp",EDGE,"E1")])],"isStart":false});
            extrude(context, id + "F7", {"entities" : qUnion([Q0, Q1, Q2, Q3]), "operationType" : NewBodyOperationType.ADD, "endBound" : BoundingType.UP_TO_SURFACE, "endBoundEntityFace" : qUnion([Q4]), "depth" : 25 * mm});
        }
        {
            var Q0;
            {var subQ0=sQuery(id+"F0.wireOp",EDGE,"E1");var subQ1=sQuery(id+"F0.wireOp",EDGE,"E0");Q0=makeQuery(id+"F7.boolean.opBoolean","MERGE",FACE,{"derivedFrom":[makeQuery(id+"F2.opExtrude","CAP_FACE",FACE,{"disambiguationData":[OSD([subQ1,subQ0])],"isStart":false}),makeQuery(id+"F7.opExtrude","CAP_FACE",FACE,{"disambiguationData":[OSD([subQ1,subQ0])],"isStart":false})]});}
            var sketch = newSketch(context, id + "F8", { "sketchPlane" : qUnion([Q0])});
            skArc(sketch, "E171.0", {"start": v(10, 55) * mm, "mid": v(0, 65) * mm, "end": v(-10, 55) * mm, "construction": true});
            skCircle(sketch, "E172", {"center": v(0, 55) * mm, "radius": 5.05 * mm});
            skCircle(sketch, "E173", {"center": v(0, 55) * mm, "radius": 2.5 * mm});
            skSolve(sketch);
        }
        {
            var Q0;
            Q0=makeQuery(id+"F8.imprint","IMPRINT",FACE,{"disambiguationData":[TD([[makeQuery(id+"F8.imprint","IMPRINT",EDGE,{"derivedFrom":sQuery(id+"F8.wireOp",EDGE,"E173")}),1.0]])]});
            extrude(context, id + "F9", {"entities" : qUnion([Q0]), "operationType" : NewBodyOperationType.REMOVE, "endBound" : BoundingType.UP_TO_NEXT, "oppositeDirection" : true, "depth" : 25 * mm});
        }
        {
            var Q0;
            Q0=makeQuery(id+"F8.imprint","IMPRINT",FACE,{"disambiguationData":[TD([[makeQuery(id+"F8.imprint","IMPRINT",EDGE,{"derivedFrom":sQuery(id+"F8.wireOp",EDGE,"E172")}),1.0]])]});
            extrude(context, id + "F10", {"entities" : qUnion([Q0]), "operationType" : NewBodyOperationType.REMOVE, "oppositeDirection" : true, "depth" : 4 * mm});
        }
        {
            var Q0;
            Q0=makeQuery(id+"F7.boolean.opBoolean","INTERSECT",EDGE,{"derivedFrom":[makeQuery(id+"F2.opExtrude","SWEPT_FACE",FACE,{"disambiguationData":[OSD([sQuery(id+"F0.wireOp",EDGE,"E1")])]}),makeQuery(id+"F7.opExtrude","SWEPT_FACE",FACE,{"disambiguationData":[OSD([sQuery(id+"F6.wireOp",EDGE,"E170.left")])]})]});
            var Q1;
            Q1=makeQuery(id+"F7.boolean.opBoolean","INTERSECT",EDGE,{"derivedFrom":[makeQuery(id+"F2.opExtrude","SWEPT_FACE",FACE,{"disambiguationData":[OSD([sQuery(id+"F0.wireOp",EDGE,"E1")])]}),makeQuery(id+"F7.opExtrude","SWEPT_FACE",FACE,{"disambiguationData":[OSD([sQuery(id+"F6.wireOp",EDGE,"E170.right")])]})]});
            fillet(context, id + "F11", {"entities" : qUnion([Q0, Q1]), "radius" : 5 * mm, "tangentPropagation" : true, "allowEdgeOverflow" : false});
        }
    });
